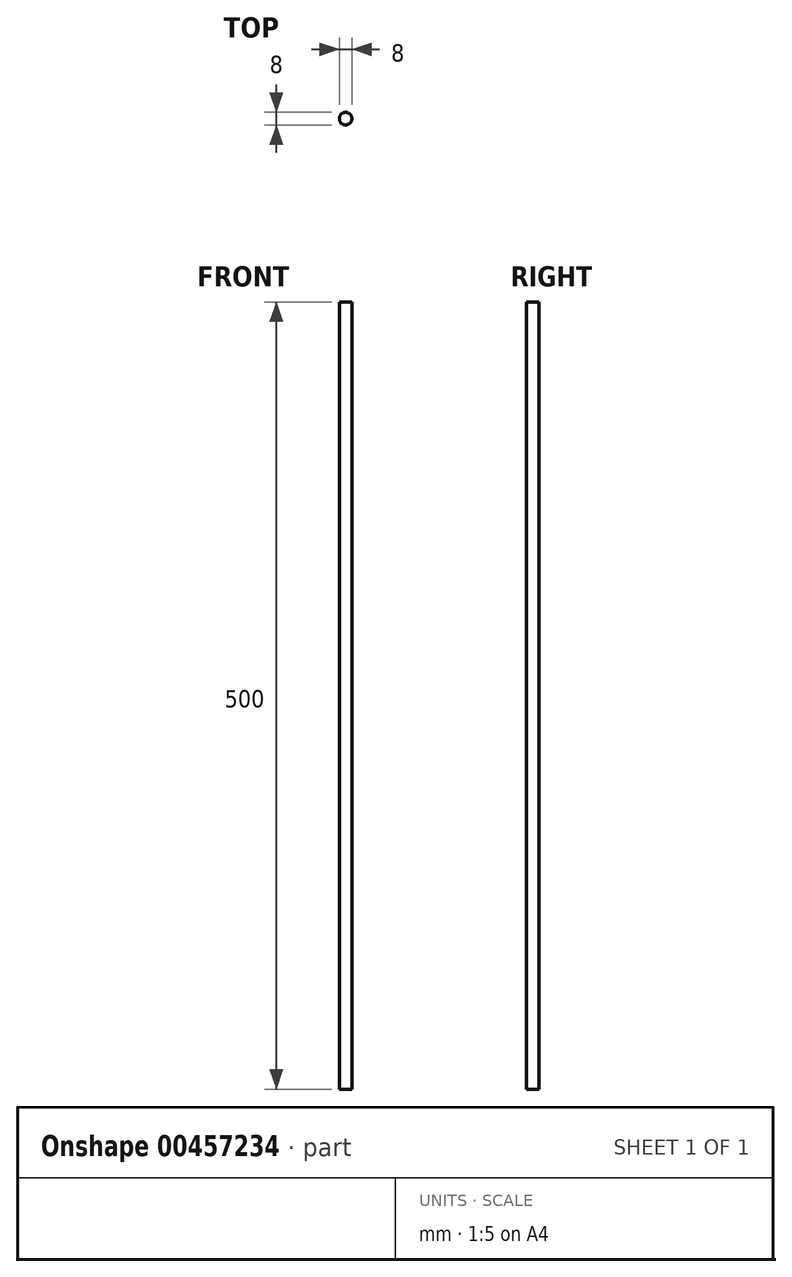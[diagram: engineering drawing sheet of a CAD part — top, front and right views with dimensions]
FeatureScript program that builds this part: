
annotation { "Feature Type Name" : "Feature", "Feature Type Description" : "" }
export const myFeature = defineFeature(function(context is Context, id is Id, definition is map)
    precondition{}
    {
        {
            var Q0;
            Q0=qCreatedBy(makeId("Top.planeOp"),FACE);
            var sketch = newSketch(context, id + "F0", { "sketchPlane" : qUnion([Q0])});
            skCircle(sketch, "E0", {"center": v(0, 0) * mm, "radius": 4 * mm});
            skSolve(sketch);
        }
        {
            var Q0;
            Q0=makeQuery(id+"F0.imprint","IMPRINT",FACE,{"disambiguationData":[TD([[makeQuery(id+"F0.imprint","IMPRINT",EDGE,{"derivedFrom":sQuery(id+"F0.wireOp",EDGE,"E0")}),1.0]])]});
            extrude(context, id + "F1", {"entities" : qUnion([Q0]), "oppositeDirection" : true, "depth" : 500 * mm});
        }
    });
